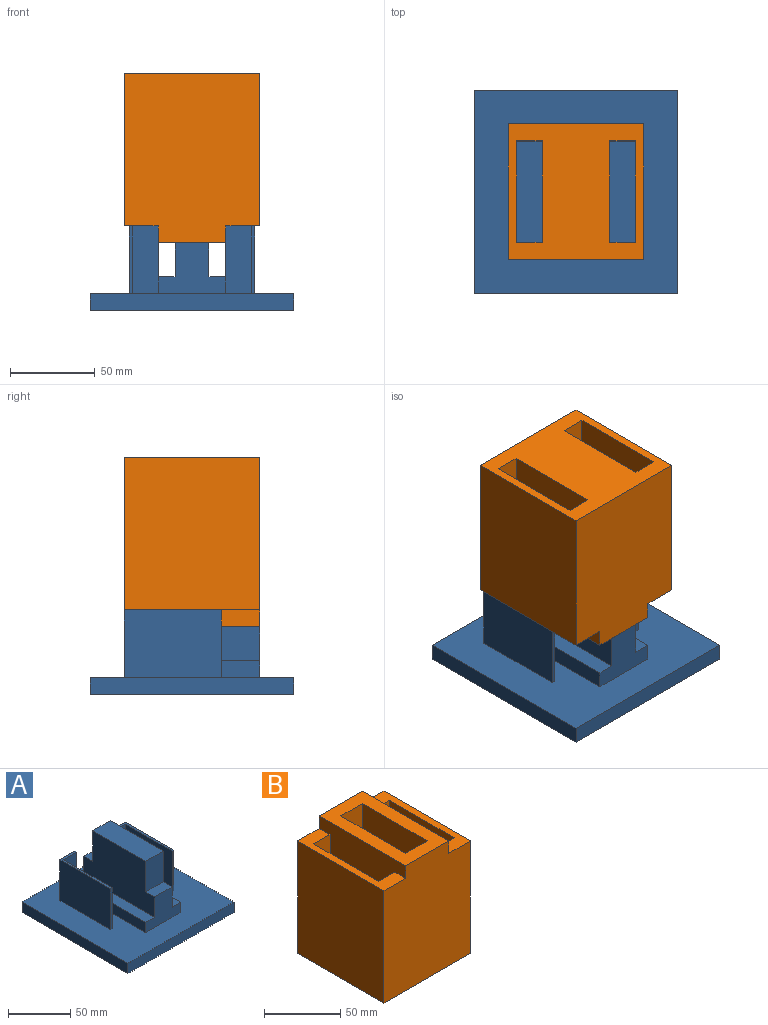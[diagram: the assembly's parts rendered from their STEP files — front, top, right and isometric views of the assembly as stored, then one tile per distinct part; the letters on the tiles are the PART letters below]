
ASSEMBLY  parts=2 mates=1
PART A: 31 faces, bbox 120x120x70 mm
  f0: plane 120x120mm, normal (0,0,1), area 10910.5mm2, adj f4,f6,f7,f8,f10,f11,f13,f14
  f1: plane 80x50mm, normal (-1,0,0), area 3400mm2, adj f3,f9,f13,f14,f15,f16,f17,f18
  f2: plane 80x50mm, normal (1,0,0), area 3400mm2, adj f3,f5,f13,f14,f15,f16,f17,f18
  f3: plane 60x20mm, normal (0,0,1), area 1200mm2, adj f1,f2,f15,f17
  f4: plane 77.89x10mm, normal (-1,0,0), area 778.9mm2, adj f0,f9,f14,f23
  f5: plane 80x10mm, normal (0,0,1), area 800mm2, adj f2,f8,f13,f14,f25
  f6: plane 120x10mm, normal (0,1,0), area 1200mm2, adj f0,f10,f11,f12
  f7: plane 120x10mm, normal (0,-1,0), area 1200mm2, adj f0,f10,f11,f12
  f8: plane 77.77x10mm, normal (1,0,0), area 777.7mm2, adj f0,f5,f14,f26
  f9: plane 80x10mm, normal (0,0,1), area 800mm2, adj f1,f4,f13,f14,f19
  f10: plane 120x10mm, normal (-1,0,0), area 1200mm2, adj f0,f6,f7,f12
  f11: plane 120x10mm, normal (1,0,0), area 1200mm2, adj f0,f6,f7,f12
  f12: plane 120x120mm, normal (0,0,-1), area 14400mm2, adj f6,f7,f10,f11
  f13: plane 74x40mm, normal (0,1,0), area 2160mm2, adj f0,f1,f2,f5,f9,f18,f19,f20
  f14: plane 40x30mm, normal (0,-1,0), area 800mm2, adj f0,f1,f2,f4,f5,f8,f9,f16
  f15: plane 30x20mm, normal (0,-1,0), area 600mm2, adj f1,f2,f3,f16
  f16: plane 20x10mm, normal (0,0,1), area 200mm2, adj f1,f2,f14,f15
  f17: plane 30x20mm, normal (0,1,0), area 600mm2, adj f1,f2,f3,f18
  f18: plane 20x10mm, normal (0,0,1), area 200mm2, adj f1,f2,f13,f17
  f19: plane 30x2.12mm, normal (1,0,0), area 63.4mm2, adj f9,f13,f23,f24
  f20: plane 57.19x40mm, normal (-1,0,0), area 2287.5mm2, adj f0,f13,f21,f24
  f21: plane 40x2mm, normal (0,-1,0), area 80mm2, adj f0,f20,f22,f24
  f22: plane 55.07x40mm, normal (1,0,0), area 2202.9mm2, adj f0,f21,f23,f24
  f23: plane 40x15mm, normal (0,-1,0), area 600mm2, adj f0,f4,f19,f22,f24
  f24: plane 57.19x17mm, normal (0,0,1), area 146.1mm2, adj f13,f19,f20,f21,f22,f23
  f25: plane 30x2.23mm, normal (-1,0,0), area 66.8mm2, adj f5,f13,f26,f30
  f26: plane 40x15mm, normal (0,-1,0), area 600mm2, adj f0,f8,f25,f27,f30
  f27: plane 52.77x40mm, normal (-1,0,0), area 2110.9mm2, adj f0,f26,f28,f30
  f28: plane 40x2mm, normal (0,-1,0), area 80mm2, adj f0,f27,f29,f30
  f29: plane 55x40mm, normal (1,0,0), area 2200mm2, adj f0,f13,f28,f30
  f30: plane 55x17mm, normal (0,0,1), area 143.4mm2, adj f13,f25,f26,f27,f28,f29
PART B: 21 faces, bbox 80x80x100 mm
  f0: plane 80x20mm, normal (0,0,1), area 700mm2, adj f4,f6,f7,f9,f18,f19,f20
  f1: plane 80x20mm, normal (0,0,1), area 700mm2, adj f4,f5,f6,f8,f15,f16,f17
  f2: plane 80x80mm, normal (0,0,-1), area 4600mm2, adj f4,f5,f6,f7,f8,f9,f15,f16
  f3: plane 80x40mm, normal (0,0,1), area 2000mm2, adj f4,f6,f8,f9,f10,f11,f12,f13
  f4: plane 100x80mm, normal (0,1,0), area 7600mm2, adj f0,f1,f2,f3,f5,f7,f8,f9
  f5: plane 90x80mm, normal (-1,0,0), area 7200mm2, adj f1,f2,f4,f6
  f6: plane 100x80mm, normal (0,-1,0), area 7600mm2, adj f0,f1,f2,f3,f5,f7,f8,f9
  f7: plane 90x80mm, normal (1,0,0), area 7200mm2, adj f0,f2,f4,f6
  f8: plane 100x80mm, normal (-1,0,0), area 6200mm2, adj f1,f2,f3,f4,f6,f15,f17
  f9: plane 100x80mm, normal (1,0,0), area 6200mm2, adj f0,f2,f3,f4,f6,f18,f19
  f10: plane 30x20mm, normal (0,-1,0), area 600mm2, adj f3,f11,f13,f14
  f11: plane 60x30mm, normal (1,0,0), area 1800mm2, adj f3,f10,f12,f14
  f12: plane 30x20mm, normal (0,1,0), area 600mm2, adj f3,f11,f13,f14
  f13: plane 60x30mm, normal (-1,0,0), area 1800mm2, adj f3,f10,f12,f14
  f14: plane 60x20mm, normal (0,0,1), area 1200mm2, adj f10,f11,f12,f13
  f15: plane 90x15mm, normal (0,1,0), area 1350mm2, adj f1,f2,f8,f16
  f16: plane 90x60mm, normal (1,0,0), area 5400mm2, adj f1,f2,f15,f17
  f17: plane 90x15mm, normal (0,-1,0), area 1350mm2, adj f1,f2,f8,f16
  f18: plane 90x15mm, normal (0,1,0), area 1350mm2, adj f0,f2,f9,f20
  f19: plane 90x15mm, normal (0,-1,0), area 1350mm2, adj f0,f2,f9,f20
  f20: plane 90x60mm, normal (-1,0,0), area 5400mm2, adj f0,f2,f18,f19
PLACE A t=(0.45,1.3,-43.56)mm fixed
PLACE B rot(axis=(1,0,0),180deg) t=(0.45,1.3,96.44)mm
MATE fastened B.f14 <-> A.f3  axis (0,0,-1) through (0.45,1.3,26.44)mm
